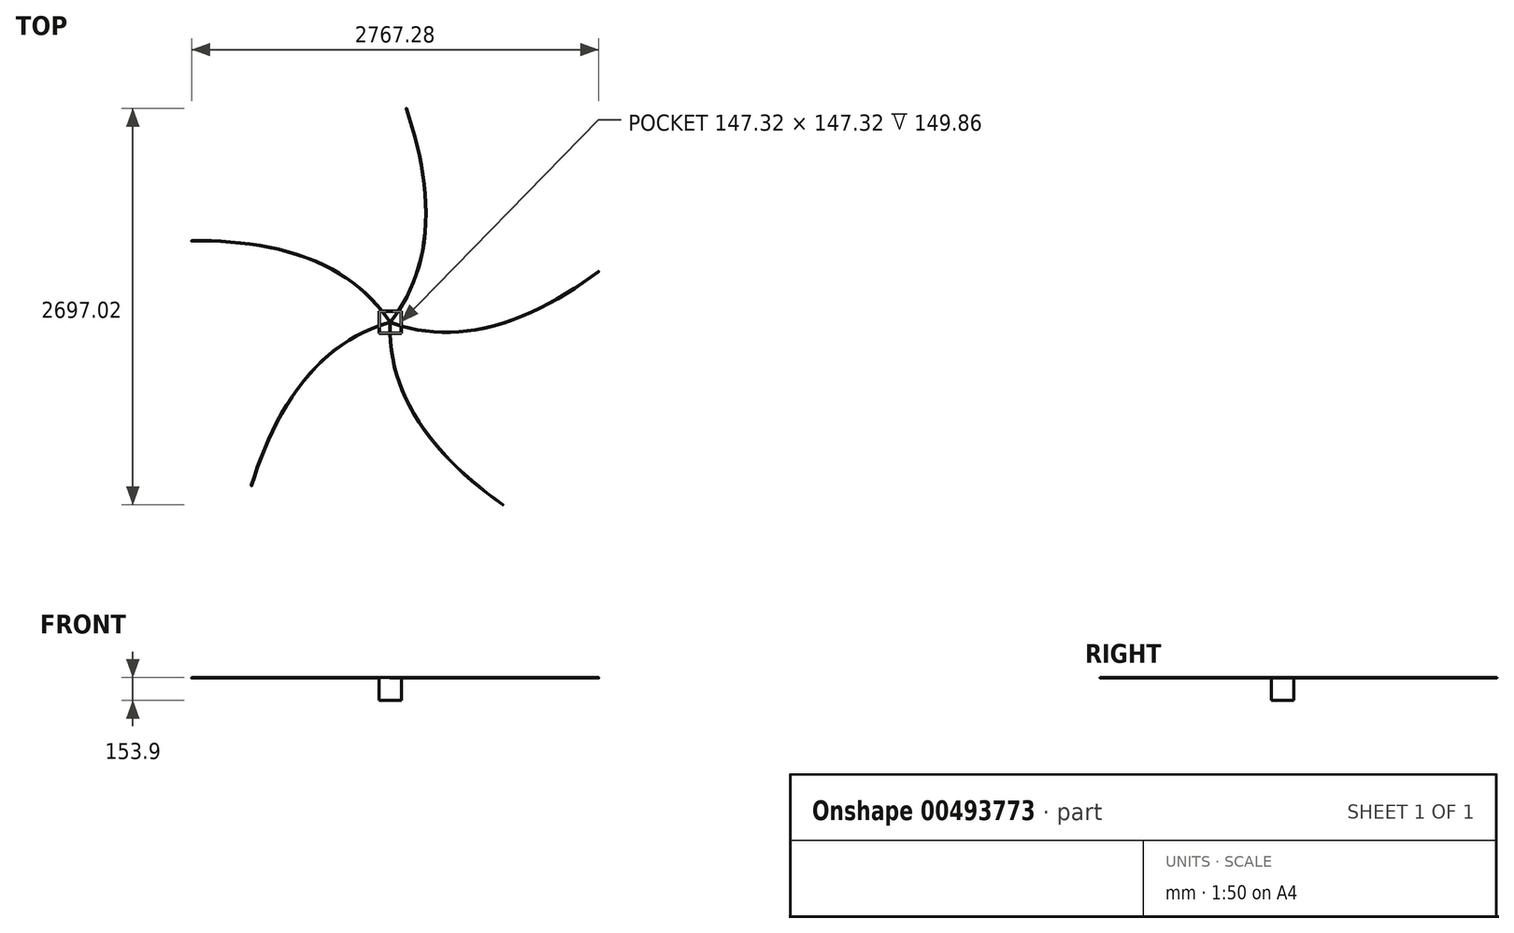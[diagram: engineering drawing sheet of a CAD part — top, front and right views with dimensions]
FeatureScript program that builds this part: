
annotation { "Feature Type Name" : "Feature", "Feature Type Description" : "" }
export const myFeature = defineFeature(function(context is Context, id is Id, definition is map)
    precondition{}
    {
        {
            var Q0;
            Q0=qCreatedBy(makeId("Top.planeOp"),FACE);
            var sketch = newSketch(context, id + "F0", { "sketchPlane" : qUnion([Q0])});
            skLineSegment(sketch, "E0.bottom", {"start": v(0, 0) * mm, "end": v(152.4, 0) * mm});
            skLineSegment(sketch, "E0.top", {"start": v(0, 152.4) * mm, "end": v(152.4, 152.4) * mm});
            skLineSegment(sketch, "E0.left", {"start": v(0, 0) * mm, "end": v(0, 152.4) * mm});
            skLineSegment(sketch, "E0.right", {"start": v(152.4, 0) * mm, "end": v(152.4, 152.4) * mm});
            skSolve(sketch);
        }
        {
            var Q0;
            Q0=qSketchRegion(id+"F0",true);
            extrude(context, id + "F1", {"entities" : qUnion([Q0]), "depth" : 152.4 * mm});
        }
        {
            var Q0;
            Q0=makeQuery(id+"F1.opExtrude","CAP_FACE",FACE,{"disambiguationData":[OSD([sQuery(id+"F0.wireOp",EDGE,"E0.bottom"),sQuery(id+"F0.wireOp",EDGE,"E0.top"),sQuery(id+"F0.wireOp",EDGE,"E0.left"),sQuery(id+"F0.wireOp",EDGE,"E0.right")])],"isStart":false});
            shell(context, id + "F2", {"entities" : qUnion([Q0]), "thickness" : 2.54 * mm});
        }
        {
            var Q0;
            Q0=makeQuery(id+"F1.opExtrude","SWEPT_BODY",BODY,{"disambiguationData":[OSD([sQuery(id+"F0.wireOp",EDGE,"E0.bottom"),sQuery(id+"F0.wireOp",EDGE,"E0.top"),sQuery(id+"F0.wireOp",EDGE,"E0.left"),sQuery(id+"F0.wireOp",EDGE,"E0.right")])]});
            transform(context, id + "F3", {"entities" : qUnion([Q0]), "transformType" : TransformType.TRANSLATION_3D, "dx" : -76.2 * mm, "dy" : -76.2 * mm, "dz" : 0 * mm, "makeCopy" : false});
        }
        {
            var Q0;
            Q0=makeQuery(id+"F2.opShell","OFFSET_FACE",FACE,{"disambiguationData":[OSD([sQuery(id+"F0.wireOp",EDGE,"E0.bottom"),sQuery(id+"F0.wireOp",EDGE,"E0.top"),sQuery(id+"F0.wireOp",EDGE,"E0.left"),sQuery(id+"F0.wireOp",EDGE,"E0.right")])]});
            var sketch = newSketch(context, id + "F4", { "sketchPlane" : qUnion([Q0])});
            skLineSegment(sketch, "E1", {"start": v(0, 0) * mm, "end": v(0, 1524) * mm});
            skPoint(sketch, "E1.endSnap0", {"position": v(0, 73.66) * mm});
            skLineSegment(sketch, "E2", {"start": v(0, 0) * mm, "end": v(-1524, 0) * mm});
            skPoint(sketch, "E2.endSnap0", {"position": v(-73.66, 0) * mm});
            skLineSegment(sketch, "E3", {"start": v(0, 0) * mm, "end": v(0, -1524) * mm});
            skPoint(sketch, "E3.endSnap0", {"position": v(0, -73.66) * mm});
            skLineSegment(sketch, "E4", {"start": v(0, 0) * mm, "end": v(1524, 0) * mm});
            skCircle(sketch, "E5", {"center": v(0, 0) * mm, "radius": 1524 * mm});
            skCircle(sketch, "E6", {"center": v(0, 0) * mm, "radius": 1069.22 * mm});
            skFitSpline(sketch, "E7", {"points": [v(0, 0) * mm, v(-822.83, -682.77) * mm], "startDerivative": vector(-1066.12, -103.57) * mm, "endDerivative": vector(-598.2, -1164.95) * mm});
            skSolve(sketch);
        }
        {
            var Q0;
            Q0=qCreatedBy(makeId("Right.planeOp"),FACE);
            var sketch = newSketch(context, id + "F5", { "sketchPlane" : qUnion([Q0])});
            skCircle(sketch, "E8", {"center": v(0, 0) * mm, "radius": 1.22 * mm});
            skLineSegment(sketch, "E9", {"start": v(0, 0) * mm, "end": v(0, 41.88) * mm});
            skSolve(sketch);
        }
        {
            var Q0;
            Q0=makeQuery(id+"F5.imprint","IMPRINT",FACE,{"disambiguationData":[TD([[makeQuery(id+"F5.imprint","IMPRINT",EDGE,{"derivedFrom":sQuery(id+"F5.wireOp",EDGE,"E8")}),1.0]])]});
            var Q1;
            Q1=sQuery(id+"F4.wireOp",EDGE,"E7");
            sweep(context, id + "F6", {"profiles" : qUnion([Q0]), "path" : qUnion([Q1])});
        }
        {
            var Q0;
            Q0=makeQuery(id+"F6.opSweep","SWEPT_BODY",BODY,{"disambiguationData":[OSD([sQuery(id+"F4.wireOp",EDGE,"E7"),sQuery(id+"F5.wireOp",EDGE,"E8")])]});
            var Q1;
            Q1=sQuery(id+"F4.wireOp",VERTEX,"E7.start");
            transform(context, id + "F7", {"entities" : qUnion([Q0]), "transformType" : TransformType.SCALE_UNIFORMLY, "scale" : 1.36, "scalePoint" : qUnion([Q1]), "makeCopy" : false});
        }
        {
            var Q0;
            Q0=makeQuery(id+"F6.opSweep","SWEPT_BODY",BODY,{"disambiguationData":[OSD([sQuery(id+"F4.wireOp",EDGE,"E7"),sQuery(id+"F5.wireOp",EDGE,"E8")])]});
            var Q1;
            Q1=sQuery(id+"F5.wireOp",EDGE,"E9");
            circularPattern(context, id + "F8", {"entities" : qUnion([Q0]), "axis" : qUnion([Q1]), "angle" : 360 * degree, "instanceCount" : 5, "equalSpace" : true});
        }
        {
            var Q0;
            Q0=makeQuery(id+"F6.opSweep","SWEPT_BODY",BODY,{"disambiguationData":[OSD([sQuery(id+"F4.wireOp",EDGE,"E7"),sQuery(id+"F5.wireOp",EDGE,"E8")])]});
            var Q1;
            Q1=makeQuery(id+"F8.opPattern","COPY",BODY,{"derivedFrom":makeQuery(id+"F6.opSweep","SWEPT_BODY",BODY,{"disambiguationData":[OSD([sQuery(id+"F4.wireOp",EDGE,"E7"),sQuery(id+"F5.wireOp",EDGE,"E8")])]}),"instanceName":"1"});
            var Q2;
            Q2=makeQuery(id+"F8.opPattern","COPY",BODY,{"derivedFrom":makeQuery(id+"F6.opSweep","SWEPT_BODY",BODY,{"disambiguationData":[OSD([sQuery(id+"F4.wireOp",EDGE,"E7"),sQuery(id+"F5.wireOp",EDGE,"E8")])]}),"instanceName":"2"});
            var Q3;
            Q3=makeQuery(id+"F8.opPattern","COPY",BODY,{"derivedFrom":makeQuery(id+"F6.opSweep","SWEPT_BODY",BODY,{"disambiguationData":[OSD([sQuery(id+"F4.wireOp",EDGE,"E7"),sQuery(id+"F5.wireOp",EDGE,"E8")])]}),"instanceName":"3"});
            var Q4;
            Q4=makeQuery(id+"F8.opPattern","COPY",BODY,{"derivedFrom":makeQuery(id+"F6.opSweep","SWEPT_BODY",BODY,{"disambiguationData":[OSD([sQuery(id+"F4.wireOp",EDGE,"E7"),sQuery(id+"F5.wireOp",EDGE,"E8")])]}),"instanceName":"4"});
            transform(context, id + "F9", {"entities" : qUnion([Q0, Q1, Q2, Q3, Q4]), "transformType" : TransformType.TRANSLATION_3D, "dx" : 0 * mm, "dy" : 0 * mm, "dz" : 153.16 * mm, "makeCopy" : false});
        }
        {
            var Q0;
            Q0=makeQuery(id+"F6.opSweep","SWEPT_BODY",BODY,{"disambiguationData":[OSD([sQuery(id+"F4.wireOp",EDGE,"E7"),sQuery(id+"F5.wireOp",EDGE,"E8")])]});
            var Q1;
            Q1=makeQuery(id+"F8.opPattern","COPY",BODY,{"derivedFrom":makeQuery(id+"F6.opSweep","SWEPT_BODY",BODY,{"disambiguationData":[OSD([sQuery(id+"F4.wireOp",EDGE,"E7"),sQuery(id+"F5.wireOp",EDGE,"E8")])]}),"instanceName":"1"});
            var Q2;
            Q2=makeQuery(id+"F8.opPattern","COPY",BODY,{"derivedFrom":makeQuery(id+"F6.opSweep","SWEPT_BODY",BODY,{"disambiguationData":[OSD([sQuery(id+"F4.wireOp",EDGE,"E7"),sQuery(id+"F5.wireOp",EDGE,"E8")])]}),"instanceName":"2"});
            var Q3;
            Q3=makeQuery(id+"F8.opPattern","COPY",BODY,{"derivedFrom":makeQuery(id+"F6.opSweep","SWEPT_BODY",BODY,{"disambiguationData":[OSD([sQuery(id+"F4.wireOp",EDGE,"E7"),sQuery(id+"F5.wireOp",EDGE,"E8")])]}),"instanceName":"3"});
            var Q4;
            Q4=makeQuery(id+"F8.opPattern","COPY",BODY,{"derivedFrom":makeQuery(id+"F6.opSweep","SWEPT_BODY",BODY,{"disambiguationData":[OSD([sQuery(id+"F4.wireOp",EDGE,"E7"),sQuery(id+"F5.wireOp",EDGE,"E8")])]}),"instanceName":"4"});
            var Q5;
            Q5=sQuery(id+"F5.wireOp",EDGE,"E9");
            transform(context, id + "F10", {"entities" : qUnion([Q0, Q1, Q2, Q3, Q4]), "transformType" : TransformType.ROTATION, "transformAxis" : qUnion([Q5]), "angle" : 10 * degree, "makeCopy" : false});
        }
    });
